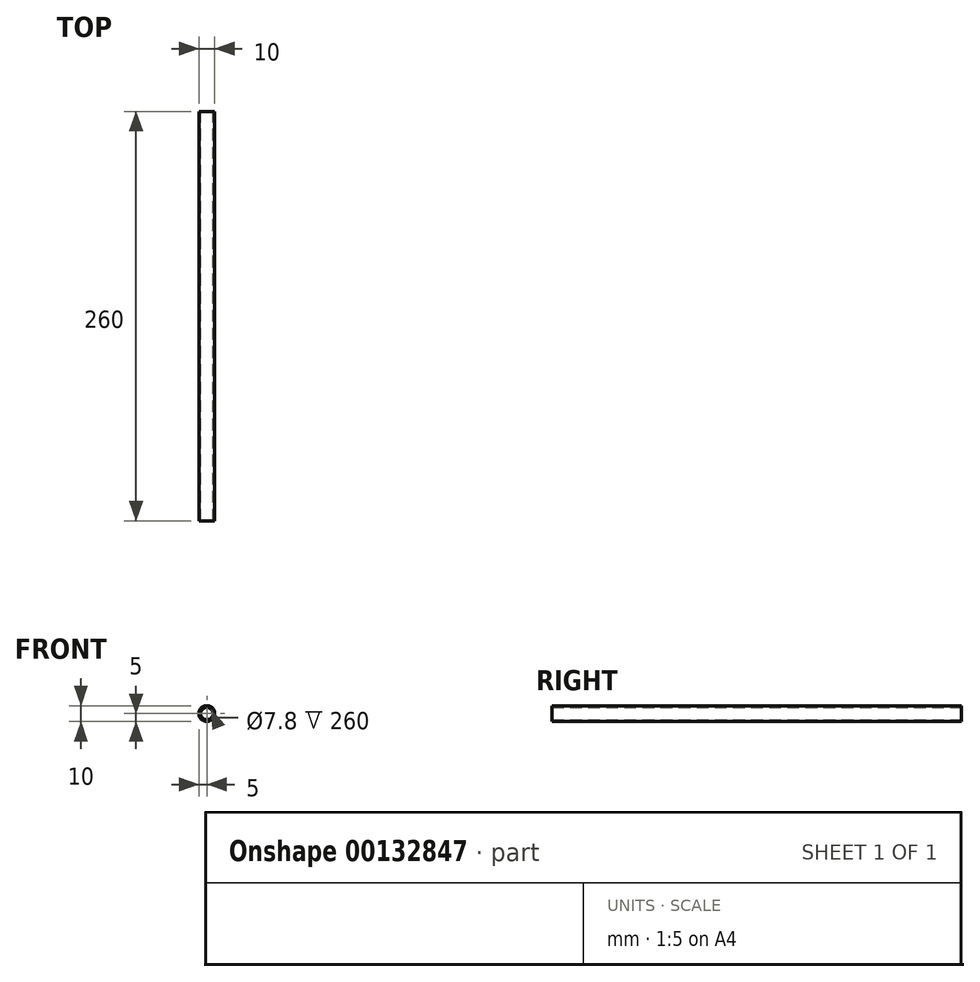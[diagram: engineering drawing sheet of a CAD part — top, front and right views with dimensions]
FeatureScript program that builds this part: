
annotation { "Feature Type Name" : "Feature", "Feature Type Description" : "" }
export const myFeature = defineFeature(function(context is Context, id is Id, definition is map)
    precondition{}
    {
        {
            var Q0;
            Q0=qCreatedBy(makeId("Front.planeOp"),FACE);
            var sketch = newSketch(context, id + "F0", { "sketchPlane" : qUnion([Q0])});
            skCircle(sketch, "E0", {"center": v(0, 0) * mm, "radius": 3.9 * mm});
            skCircle(sketch, "E1", {"center": v(0, 0) * mm, "radius": 5 * mm});
            skSolve(sketch);
        }
        {
            var Q0;
            Q0=makeQuery(id+"F0.imprint","IMPRINT",FACE,{"disambiguationData":[TD([[makeQuery(id+"F0.imprint","IMPRINT",EDGE,{"derivedFrom":sQuery(id+"F0.wireOp",EDGE,"E0")}),-1.0]])]});
            extrude(context, id + "F1", {"entities" : qUnion([Q0]), "depth" : 260 * mm});
        }
    });
